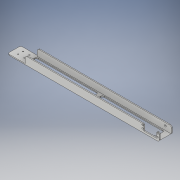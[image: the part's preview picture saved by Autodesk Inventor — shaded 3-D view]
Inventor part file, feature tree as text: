
AUTODESK INVENTOR PART (.ipt)
format: ipt  version: 2017 (Build 210142000, 142)  size: 254,976 bytes
history: native  units: in
note: dims shown in document units (in); Inventor stores cm internally (conversion verified against a paired STEP export)
features: sketch x6, extrude x5, projected_geometry x5, fillet x4, hole x1
ambient origin geometry x8: Origin, YZ Plane, XZ Plane, XY Plane, X Axis, Y Axis, Z Axis, Center Point
bodies: Solid1 (feature_tree)
feature tree (21):
  extrude  "Extrusion1"  Depth=1.685in
  extrude  "Extrusion2"  Depth=1.435in
  extrude  "Extrusion3"  Depth=19.5in TaperAngle=0.0deg
  fillet  "Fillet1"  Radius=0.35in
  fillet  "Fillet2"  Radius=1.0in
  extrude  "Extrusion5"  Depth=2.0in
  fillet  "Fillet3"  Radius=0.19in
  extrude  "Extrusion6"  Depth=0.3937in
  fillet  "Fillet4"  Radius=0.3937in
  hole  "Hole1"  [1 undecoded]
  sketch  "Sketch1"  dims[d0=1.0in d1=1.685in]
  sketch  "Sketch2"  dims[d2=0.875in d3=1.435in]
  projected_geometry  "Projected Loop1"
  sketch  "Sketch3"  dims[d4=0.125in d5=19.5in d6=0.0in d7=0.35in d8=1.0in]
  projected_geometry  "Projected Loop2"
  sketch  "Sketch6"  dims[d9=0.75in d10=2.0in d11=0.19in]
  projected_geometry  "Projected Loop4"
  sketch  "Sketch7"  dims[d12=0.19in d13=0.164in d14=0.3937in]
  projected_geometry  "Projected Loop5"
  sketch  "Sketch8"  dims[d15=0.19in d16=0.19in d19=0.5in d20=0.0in d21=0.25in d22=0.776in d23=0.361in d24=0.5in d25=0.0in d26=0.197in d27=0.197in d28=1.9488in d29=1.9488in d30=0.3937in d43=0.125in d44=0.25in d46=2.25in d47=0.875in d48=5.0in d49=0.0in d50=0.25in d52=1.685in d53=0.25in d54=0.25in d55=2.25in d56=17.0in d57=8.0in d58=8.0in d59=0.25in d60=0.25in d61=0.5in d62=5.0in d63=0.0in d64=0.25in d70=0.8051in d71=0.6299in d72=0.4772in d73=0.7785in d74=0.1457in d75=0.75in d76=0.375in d77=0.25in d78=0.5635in d79=1.0in d80=0.8108in]
  projected_geometry  "Projected Loop6"
note: 1 required parameter value undecoded (feature->parameter linkage not recoverable at this tier; creation-order binding heuristic only, values carry confidence <= 0.55)
